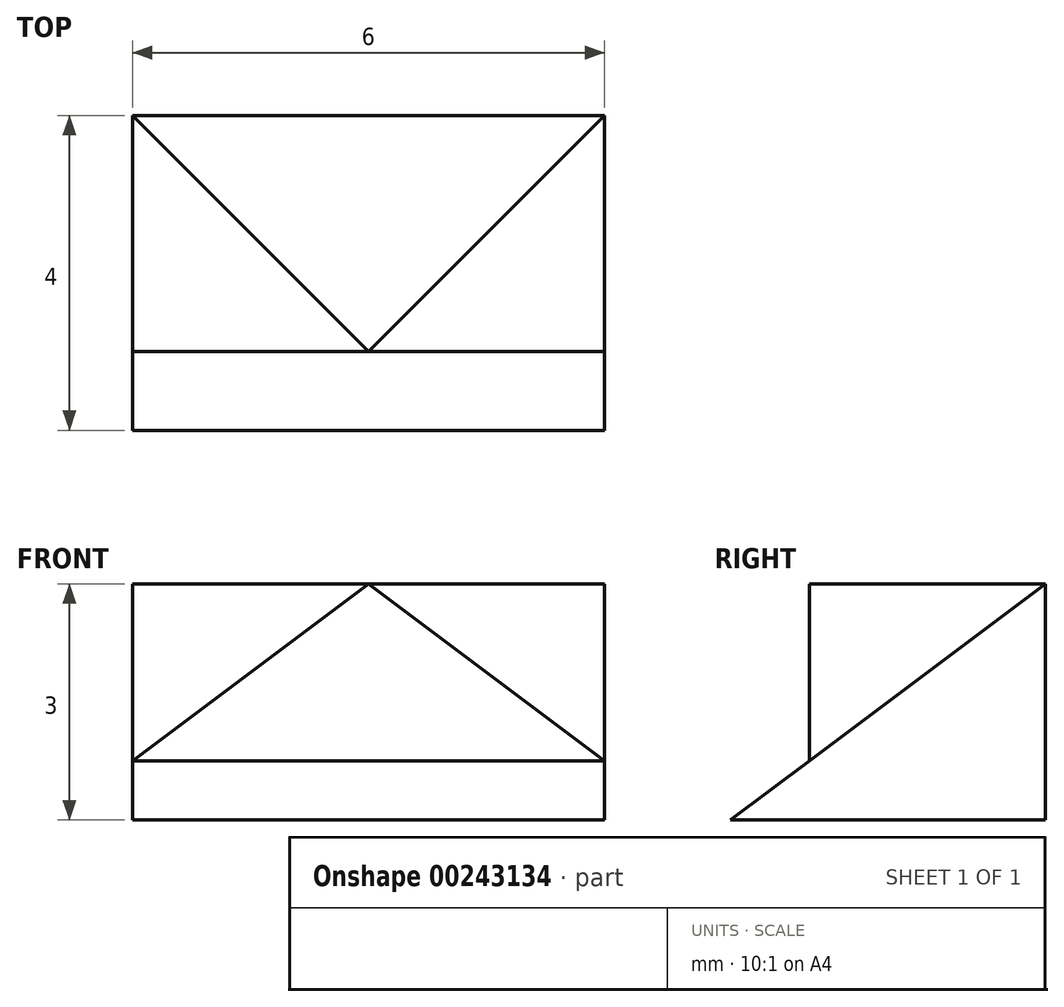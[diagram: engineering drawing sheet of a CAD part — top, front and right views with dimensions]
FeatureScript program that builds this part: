
annotation { "Feature Type Name" : "Feature", "Feature Type Description" : "" }
export const myFeature = defineFeature(function(context is Context, id is Id, definition is map)
    precondition{}
    {
        {
            var Q0;
            Q0=qCreatedBy(makeId("Right.planeOp"),FACE);
            var sketch = newSketch(context, id + "F0", { "sketchPlane" : qUnion([Q0])});
            skLineSegment(sketch, "E0", {"start": v(0, 0) * mm, "end": v(4, 0) * mm});
            skLineSegment(sketch, "E1", {"start": v(4, 0) * mm, "end": v(4, 3) * mm});
            skLineSegment(sketch, "E2", {"start": v(4, 3) * mm, "end": v(0, 0) * mm});
            skSolve(sketch);
        }
        {
            var Q0;
            Q0 = qSketchRegion(id + "F0", true);
            extrude(context, id + "F1", {"entities" : qUnion([Q0]), "depth" : 6 * mm});
        }
        {
            var Q0;
            Q0=makeQuery(id+"F1.opExtrude","CAP_FACE",FACE,{"disambiguationData":[OSD([sQuery(id+"F0.wireOp",EDGE,"E0"),sQuery(id+"F0.wireOp",EDGE,"E1"),sQuery(id+"F0.wireOp",EDGE,"E2")])],"isStart":false});
            var sketch = newSketch(context, id + "F2", { "sketchPlane" : qUnion([Q0])});
            skLineSegment(sketch, "E3", {"start": v(4, 3) * mm, "end": v(1, 3) * mm});
            skLineSegment(sketch, "E4", {"start": v(1, 3) * mm, "end": v(1, 0.75) * mm});
            skLineSegment(sketch, "E5", {"start": v(4, 3) * mm, "end": v(1, 0.75) * mm});
            skSolve(sketch);
        }
        {
            var Q0;
            Q0 = qSketchRegion(id + "F2", true);
            extrude(context, id + "F3", {"entities" : qUnion([Q0]), "operationType" : NewBodyOperationType.ADD, "oppositeDirection" : true, "depth" : 6 * mm});
        }
        {
            var Q0;
            Q0=makeQuery(id+"F3.opExtrude","SWEPT_FACE",FACE,{"disambiguationData":[OSD([sQuery(id+"F2.wireOp",EDGE,"E3")])]});
            var sketch = newSketch(context, id + "F4", { "sketchPlane" : qUnion([Q0])});
            skPoint(sketch, "E6", {"position": v(3, 1) * mm});
            skSolve(sketch);
        }
        {
            var Q0;
            Q0=makeQuery(id+"F3.opExtrude","SWEPT_EDGE",EDGE,{"disambiguationData":[OSD([sQuery(id+"F2.wireOp",EDGE,"E3"),sQuery(id+"F2.wireOp",EDGE,"E4")])]});
            cPoint(context, id + "F5", {"entities" : qUnion([Q0]), "parameter" : 0.5});
        }
        {
            var Q0;
            {var subQ0=sQuery(id+"F0.wireOp",EDGE,"E1");Q0=makeQuery(id+"F3.boolean.opBoolean","MERGE",VERTEX,{"derivedFrom":[makeQuery(id+"F1.opExtrude","CAP_VERTEX",VERTEX,{"disambiguationData":[OSD([subQ0,sQuery(id+"F0.wireOp",EDGE,"E2")])],"isStart":false}),makeQuery(id+"F3.opExtrude","CAP_VERTEX",VERTEX,{"disambiguationData":[OSD([subQ0,sQuery(id+"F2.wireOp",EDGE,"E3"),sQuery(id+"F2.wireOp",EDGE,"E5")])],"isStart":true})]});}
            var Q1;
            Q1=makeQuery(id+"F3.opExtrude","CAP_VERTEX",VERTEX,{"disambiguationData":[OSD([sQuery(id+"F0.wireOp",EDGE,"E2"),sQuery(id+"F2.wireOp",EDGE,"E4"),sQuery(id+"F2.wireOp",EDGE,"E5")])],"isStart":true});
            var Q2;
            Q2 = qCreatedBy(id + "F5" ,VERTEX);
            cPlane(context, id + "F6", {"entities" : qUnion([Q0, Q1, Q2]), "cplaneType" : CPlaneType.THREE_POINT, "offset" : 25 * mm, "width" : 150 * mm, "height" : 150 * mm});
        }
        {
            var Q0;
            Q0=qCreatedBy(id+"F6.planeOp",FACE);
            var sketch = newSketch(context, id + "F7", { "sketchPlane" : qUnion([Q0])});
            skPoint(sketch, "E7.1", {"position": v(5.14, 5) * mm});
            skPoint(sketch, "E7.2", {"position": v(5.14, 1.25) * mm});
            skPoint(sketch, "E8.0", {"position": v(1.65, 2.6) * mm});
            skLineSegment(sketch, "E9", {"start": v(5.14, 5) * mm, "end": v(1.65, 2.6) * mm});
            skLineSegment(sketch, "E10", {"start": v(5.14, 1.25) * mm, "end": v(5.14, 5) * mm});
            skLineSegment(sketch, "E11", {"start": v(1.65, 2.6) * mm, "end": v(5.14, 1.25) * mm});
            skSolve(sketch);
        }
        {
            var Q0;
            Q0 = qSketchRegion(id + "F7", true);
            extrude(context, id + "F8", {"entities" : qUnion([Q0]), "operationType" : NewBodyOperationType.REMOVE, "depth" : 25 * mm});
        }
        {
            var Q0;
            {var subQ0=sQuery(id+"F0.wireOp",EDGE,"E1");Q0=makeQuery(id+"F3.boolean.opBoolean","MERGE",VERTEX,{"derivedFrom":[makeQuery(id+"F1.opExtrude","CAP_VERTEX",VERTEX,{"disambiguationData":[OSD([subQ0,sQuery(id+"F0.wireOp",EDGE,"E2")])],"isStart":true}),makeQuery(id+"F3.opExtrude","CAP_VERTEX",VERTEX,{"disambiguationData":[OSD([subQ0,sQuery(id+"F2.wireOp",EDGE,"E3"),sQuery(id+"F2.wireOp",EDGE,"E5")])],"isStart":false})]});}
            var Q1;
            Q1=makeQuery(id+"F3.opExtrude","CAP_VERTEX",VERTEX,{"disambiguationData":[OSD([sQuery(id+"F0.wireOp",EDGE,"E2"),sQuery(id+"F2.wireOp",EDGE,"E4"),sQuery(id+"F2.wireOp",EDGE,"E5")])],"isStart":false});
            var Q2;
            Q2=sQuery(id+"F4.wireOp",VERTEX,"E6");
            cPlane(context, id + "F9", {"entities" : qUnion([Q0, Q1, Q2]), "cplaneType" : CPlaneType.THREE_POINT, "offset" : 25 * mm, "width" : 150 * mm, "height" : 150 * mm});
        }
        {
            var Q0;
            Q0=qCreatedBy(id+"F9.planeOp",FACE);
            var sketch = newSketch(context, id + "F10", { "sketchPlane" : qUnion([Q0])});
            skPoint(sketch, "E12.0", {"position": v(0, -5) * mm});
            skPoint(sketch, "E12.2", {"position": v(0, -1.25) * mm});
            skLineSegment(sketch, "E13", {"start": v(0, -5) * mm, "end": v(0, -1.25) * mm});
            skPoint(sketch, "E14.0", {"position": v(3.5, -2.6) * mm});
            skLineSegment(sketch, "E15", {"start": v(0, -5) * mm, "end": v(3.5, -2.6) * mm});
            skLineSegment(sketch, "E16", {"start": v(0, -1.25) * mm, "end": v(3.5, -2.6) * mm});
            skSolve(sketch);
        }
        {
            var Q0;
            Q0 = qSketchRegion(id + "F10", true);
            extrude(context, id + "F11", {"entities" : qUnion([Q0]), "operationType" : NewBodyOperationType.REMOVE, "oppositeDirection" : true, "depth" : 25 * mm});
        }
    });
